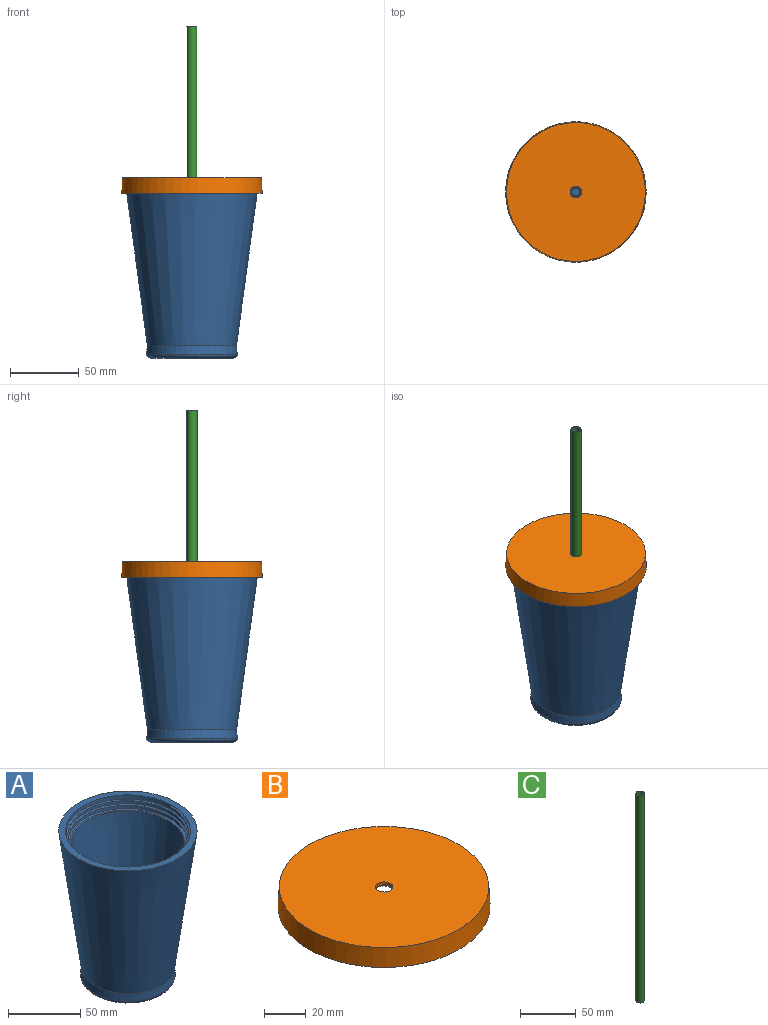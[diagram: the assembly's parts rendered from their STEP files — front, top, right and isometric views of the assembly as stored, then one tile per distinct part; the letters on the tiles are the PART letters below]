
ASSEMBLY  parts=3 mates=2
PART A: 13 faces, bbox 96.4x96.4x124.6 mm
  f0: cone r=43.33mm half-angle=7.7deg, axis (0,0,1), area 1986.2mm2, adj f6,f7,f10,f11,f12
  f1: plane 41.65x41.65mm, normal (0,0,1), area 1362.2mm2, adj f9
  f2: plane 60.62x60.62mm, normal (0,0,-1), area 2886.1mm2, adj f3
  f3: torus R=30.31mm, axis (0,0,-1), area 839.2mm2, adj f2,f4
  f4: cone r=32.84mm half-angle=4.2deg, axis (0,0,-1), area 1266.3mm2, adj f3,f5
  f5: cone r=48.01mm half-angle=7.7deg, axis (0,0,1), area 29389.5mm2, adj f4,f6
  f6: plane 96.01x96.01mm, normal (0,0,1), area 1341.8mm2, adj f0,f5
  f7: plane 84.13x83.59mm, normal (0,0,1), area 516.8mm2, adj f0,f8,f10,f11
  f8: cone r=39.6mm half-angle=7.7deg, axis (0,0,1), area 21058.7mm2, adj f7,f9
  f9: torus R=20.82mm, axis (0,0,-1), area 1094.9mm2, adj f1,f8
  f10: bspline ~87.04x86.93mm, area 1100.5mm2, adj f0,f7,f11,f12
  f11: bspline ~86.7x86.59mm, area 1032.9mm2, adj f0,f7,f10,f12
  f12: plane 1.34x1.26mm, normal (0,1,0), area 0.8mm2, adj f0,f10,f11
PART B: 14 faces, bbox 102.7x102.7x16.9 mm
  f0: cylinder r=39.22mm len=78.44mm, axis (0,0,1), area 2214.7mm2, adj f6,f7,f11,f12,f13
  f1: plane 100.79x100.79mm, normal (0,0,1), area 7922.9mm2, adj f2,f10
  f2: cylinder r=4.19mm len=8.38mm, axis (0,0,1), area 44.8mm2, adj f1,f3
  f3: torus R=5.46mm, axis (0,0,1), area 58.3mm2, adj f2,f4
  f4: plane 74.73x74.73mm, normal (0,0,-1), area 4292mm2, adj f3,f5
  f5: cylinder r=37.36mm len=74.73mm, axis (0,0,1), area 3088.8mm2, adj f4,f6
  f6: plane 78.44x78.44mm, normal (0,0,-1), area 446.1mm2, adj f0,f5
  f7: plane 96.35x96.35mm, normal (0,0,-1), area 2286mm2, adj f0,f8,f12,f13
  f8: cone r=48.21mm half-angle=2.9deg, axis (0,0,-1), area 2526.3mm2, adj f7,f9
  f9: plane 101.95x101.95mm, normal (0,0,-1), area 862.7mm2, adj f8,f10
  f10: cone r=50.39mm half-angle=2.9deg, axis (0,0,-1), area 3615.7mm2, adj f1,f9
  f11: plane 1.47x1.28mm, normal (0,-1,0), area 0.9mm2, adj f0,f12,f13
  f12: bspline ~93.52x80.99mm, area 1075.8mm2, adj f0,f7,f11,f13
  f13: bspline ~93.52x80.99mm, area 1013.5mm2, adj f0,f7,f11,f12
PART C: 4 faces, bbox 7.3x7.3x228.6 mm
  f0: cylinder r=3.02mm len=228.6mm, axis (0,0,-1), area 4341.5mm2, adj f2,f3
  f1: cylinder r=3.66mm len=228.6mm, axis (0,0,-1), area 5253.5mm2, adj f2,f3
  f2: plane 7.32x7.32mm, normal (0,0,1), area 13.3mm2, adj f0,f1
  f3: plane 7.32x7.32mm, normal (0,0,-1), area 13.3mm2, adj f0,f1
PLACE A rot(axis=(0,0,-1),128.4deg) t=(53.06,18.46,-116.36)mm
PLACE B t=(53.06,18.46,14.54)mm
PLACE C t=(53.06,18.46,10.22)mm
MATE slider B.f0 <-> C.f1  axis (0,0,1) through (53.06,18.46,14.54)mm
MATE cylindrical B.f0 <-> A.f0  axis (0,0,1) through (53.06,18.46,4.99)mm
